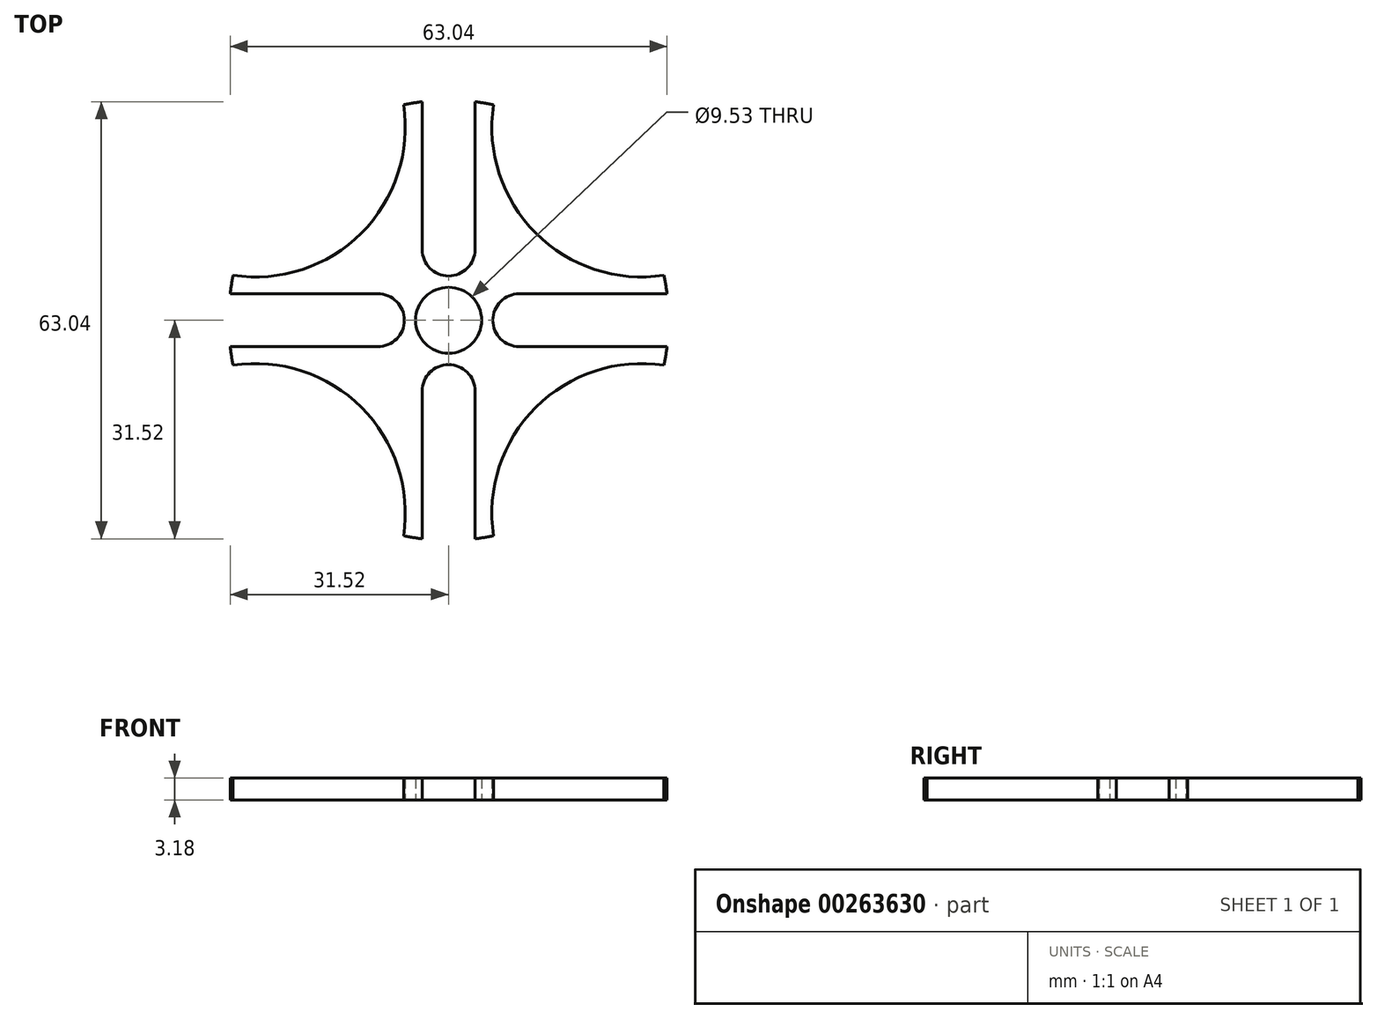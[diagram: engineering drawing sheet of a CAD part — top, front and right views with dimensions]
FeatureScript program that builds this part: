
annotation { "Feature Type Name" : "Feature", "Feature Type Description" : "" }
export const myFeature = defineFeature(function(context is Context, id is Id, definition is map)
    precondition{}
    {
        {
            var Q0;
            Q0=qCreatedBy(makeId("Top.planeOp"),FACE);
            var sketch = newSketch(context, id + "F0", { "sketchPlane" : qUnion([Q0])});
            skArc(sketch, "E0", {"start": v(-31.08, 6.5) * mm, "mid": v(-31.33, 5.16) * mm, "end": v(-31.52, 3.81) * mm});
            skCircle(sketch, "E1", {"center": v(0, 0) * mm, "radius": 4.76 * mm});
            skArc(sketch, "E2", {"start": v(6.5, 31.08) * mm, "mid": v(12.57, 12.57) * mm, "end": v(31.08, 6.5) * mm});
            skArc(sketch, "E3", {"start": v(31.08, -6.5) * mm, "mid": v(12.57, -12.57) * mm, "end": v(6.5, -31.08) * mm});
            skArc(sketch, "E4", {"start": v(-6.5, -31.08) * mm, "mid": v(-12.57, -12.57) * mm, "end": v(-31.08, -6.5) * mm});
            skArc(sketch, "E5", {"start": v(-31.08, 6.5) * mm, "mid": v(-12.57, 12.57) * mm, "end": v(-6.5, 31.08) * mm});
            skLineSegment(sketch, "E6", {"start": v(3.81, -10.2) * mm, "end": v(3.81, -31.52) * mm});
            skLineSegment(sketch, "E7", {"start": v(-3.81, -10.2) * mm, "end": v(-3.8, -31.52) * mm});
            skArc(sketch, "E8", {"start": v(3.81, -10.2) * mm, "mid": v(0, -6.4) * mm, "end": v(-3.81, -10.2) * mm});
            skLineSegment(sketch, "E9", {"start": v(-10.2, -3.81) * mm, "end": v(-31.52, -3.81) * mm});
            skLineSegment(sketch, "E10", {"start": v(-10.2, 3.81) * mm, "end": v(-31.52, 3.81) * mm});
            skArc(sketch, "E11", {"start": v(-10.2, -3.81) * mm, "mid": v(-6.4, 0) * mm, "end": v(-10.2, 3.81) * mm});
            skLineSegment(sketch, "E12", {"start": v(-3.81, 10.2) * mm, "end": v(-3.81, 31.52) * mm});
            skLineSegment(sketch, "E13", {"start": v(3.81, 10.2) * mm, "end": v(3.81, 31.52) * mm});
            skArc(sketch, "E14", {"start": v(-3.81, 10.2) * mm, "mid": v(0, 6.4) * mm, "end": v(3.81, 10.2) * mm});
            skLineSegment(sketch, "E15", {"start": v(10.2, 3.81) * mm, "end": v(31.52, 3.81) * mm});
            skLineSegment(sketch, "E16", {"start": v(10.2, -3.81) * mm, "end": v(31.52, -3.81) * mm});
            skArc(sketch, "E17", {"start": v(10.2, 3.81) * mm, "mid": v(6.4, 0) * mm, "end": v(10.2, -3.81) * mm});
            skArc(sketch, "E18.trimOffspring", {"start": v(6.5, 31.08) * mm, "mid": v(5.16, 31.33) * mm, "end": v(3.8, 31.52) * mm});
            skArc(sketch, "E19.trimOffspring", {"start": v(31.08, -6.5) * mm, "mid": v(31.33, -5.16) * mm, "end": v(31.52, -3.81) * mm});
            skArc(sketch, "E20.trimOffspring", {"start": v(-6.5, -31.08) * mm, "mid": v(-5.16, -31.33) * mm, "end": v(-3.8, -31.52) * mm});
            skArc(sketch, "E21.trimOffspring", {"start": v(-31.52, -3.81) * mm, "mid": v(-31.33, -5.16) * mm, "end": v(-31.08, -6.5) * mm});
            skArc(sketch, "E22.trimOffspring", {"start": v(31.52, 3.8) * mm, "mid": v(31.33, 5.16) * mm, "end": v(31.08, 6.5) * mm});
            skArc(sketch, "E23.trimOffspring", {"start": v(-3.81, 31.52) * mm, "mid": v(-5.16, 31.33) * mm, "end": v(-6.5, 31.08) * mm});
            skArc(sketch, "E24.trimOffspring", {"start": v(3.8, -31.52) * mm, "mid": v(5.16, -31.33) * mm, "end": v(6.5, -31.08) * mm});
            skSolve(sketch);
        }
        {
            var Q0;
            Q0=makeQuery(id+"F0.imprint","IMPRINT",FACE,{"disambiguationData":[TD([[makeQuery(id+"F0.imprint","IMPRINT",EDGE,{"derivedFrom":sQuery(id+"F0.wireOp",EDGE,"E0")}),1.0]])]});
            extrude(context, id + "F1", {"entities" : qUnion([Q0]), "depth" : 3.17 * mm});
        }
    });
